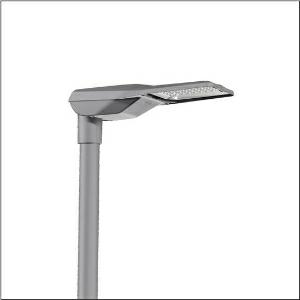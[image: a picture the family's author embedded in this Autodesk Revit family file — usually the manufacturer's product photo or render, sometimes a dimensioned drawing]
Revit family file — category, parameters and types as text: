
# Revit family: streetlight_sl_21_iq_mini___pl52_5xe2h31g08gb_d0f1
name_source: partatom
category: Lighting Fixtures
units: mm (PartAtom-declared; Revit-internal decimal feet)

## family parameters
Cut with Voids When Loaded = No
Host = Face
Light Source = No
Part Type = Normal
Room Calculation Point = No
Round Connector Dimension = Use Diameter
Shared = No

## types (1)
- --- (1 x LED, 5580 lm, 37.1 W, 3000K)
    Apparent Load = 37 VA
    CIE Flux Codes = 27 59 98 100 100
    Color Rendering = 70
    Color Temperature = 3000K
    Default Elevation = 1800 mm
    Description = Streetlight SL 21 iQ mini, mast luminaire, primary light control with lens, of PMMA, primary optical cover: cover, of toughened safety glass, transparent, light distribution: PL52, light emission: direct distribution, primary light characteristic: asymmetric, installation type: post-top, side-entry, LED, High Power LED, rated luminous flux: 5.580lm, luminous efficacy: 150lm/W, light colour: 730, colour temperature: 3000K, control gear: iQ Street-Remote, control: Street-Remote, Auto-Match, Temp-Guard, Lumen-Switch, Night-Set, Smart-Wire, Light-Fading, Desk-Remote (wireless, voltage-free reading and setting of iQ features in the workshop via application-optimized NFC function/RFID function), optimised constant luminous flux control (CLO 2.0), pre-setting: linear dimming characteristic, mains connection: 220..240V, AC, 50/60Hz, start of lifetime: 37W, end of service life: 39W, reduction: 18W, luminaire housing, of diecast aluminium, powder-coated, Siteco® metallic grey (DB 702S), corrosivity category C5 mid according to DIN EN ISO 12944, please order mast flange separately, inclination adjustable: 0°, 5°, 10°, 15°, sealing non-destructively replaceable, multi-level sealing system, length: 628mm, width: 235mm, height: 110mm, mast flange for spigot size: 42mm (side-entry): 5XC10008XM4, 60/48mm (side-entry/post-top): 5XC10108XM2, 76/60mm (side-entry/post-top): 5XC10108XM1, mounting height: 4..8m, protection rating (complete): IP66, insulation class (complete): insulation class II (safety insulation), certification: CE, ENEC, ENEC+, VDE, impact resistance: IK10, permissible operating ambient temperature for outdoor applications: -40..+50°C, standard-compliant lighting for roads and squares, packaging unit: 1 piece

Light Distribution: PL52
    Height = 110 mm
    Lamp = 1 x LED
    Lamp Light Flux = 5580 lm
    Lamp Power = 37.1 W
    Lamp count = 1
    Length = 625 mm
    Luminous efficacy = 150 lm/W
    Manufacturer = Siteco
    ModVariant = No
    Model = 5XE2H31G08GB
    Number of Poles = 1
    OnlyDefault = Yes
    Power Factor = 1
    Product Name = Streetlight SL 21 iQ mini | PL52
    Product group = mast luminaire | pylon top
    ProductGroupID = 6100
    Protection Class = Protection class II
    Protection Degree = IP 66
    RLX_Detail_Level = 1
    RLX_Emergency_Light_Flux = 0 lm
    RLX_Emergency_Type = 0
    RLX_Emergency_Type_DB = No
    RlxData = <blob elided: 35861 chars, md5=8ad954f5>
    Socket = socket
    Standby Power = 0 W
    System Light Flux = 5580 lm
    System Power = 37 W
    Type Comments = factory setting: luminous flux: 100 % | dim-lin: 254 | 385 mA
    Type Image = l_1003519.jpg
    URL = http://relux.com
    VarID = @adj_190318
    Voltage = 0 V
    Weight = 0.00 kg
    Width = 234 mm

## geometry (parser evidence)
native form markers: Blend x4, Sweep x9
no freeform markers — native parametric forms only
